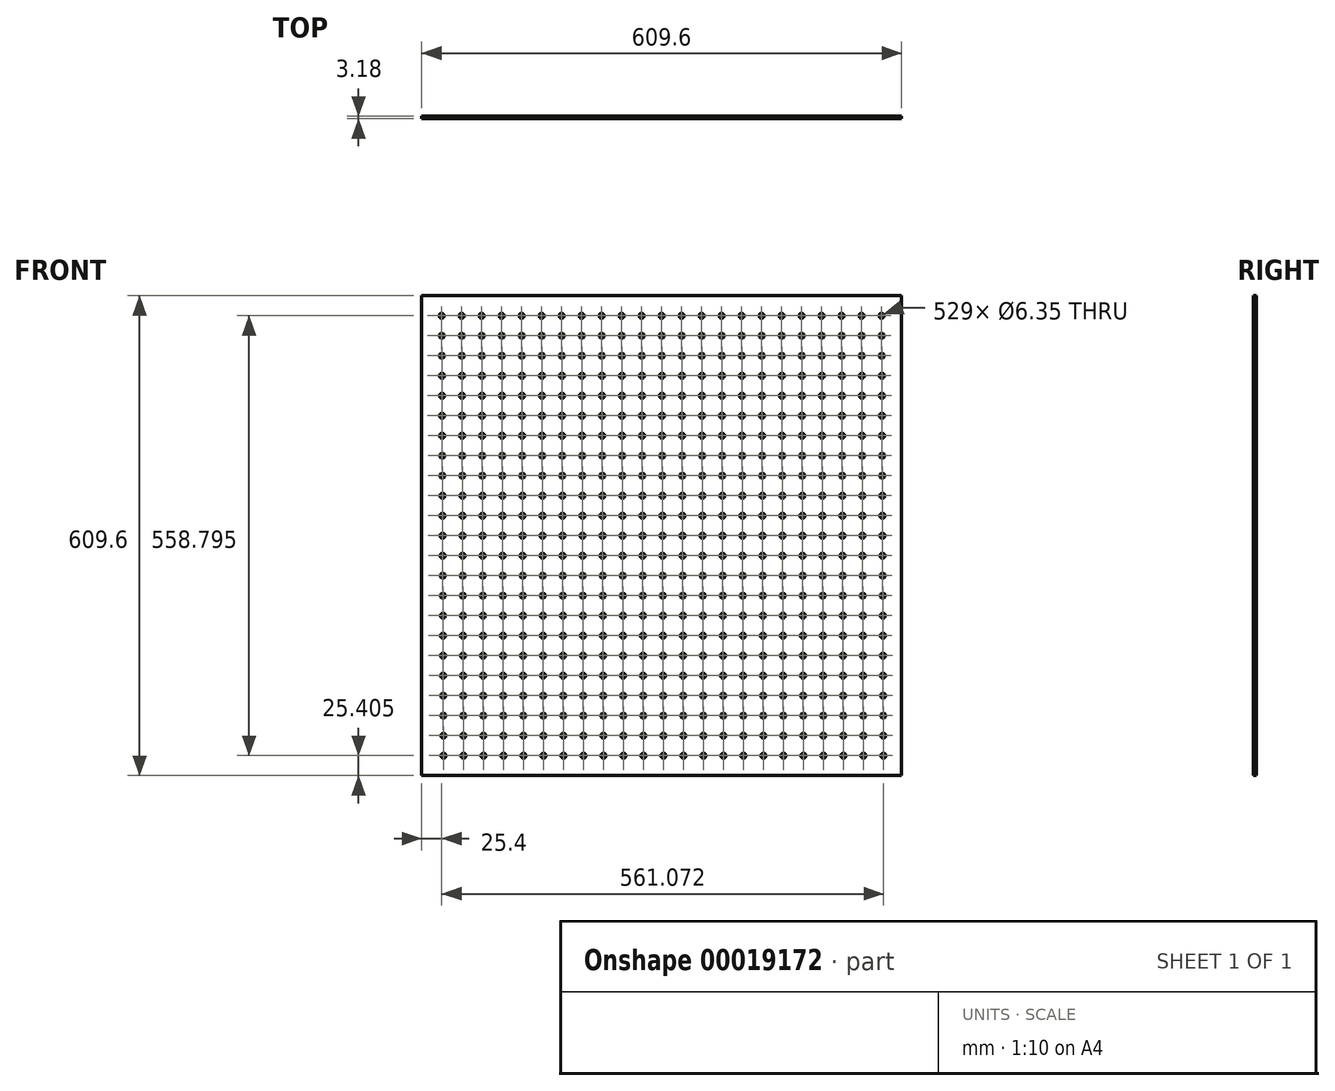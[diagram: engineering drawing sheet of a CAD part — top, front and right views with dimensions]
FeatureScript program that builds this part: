
annotation { "Feature Type Name" : "Feature", "Feature Type Description" : "" }
export const myFeature = defineFeature(function(context is Context, id is Id, definition is map)
    precondition{}
    {
        {
            var Q0;
            Q0=qCreatedBy(makeId("Front.planeOp"),FACE);
            var sketch = newSketch(context, id + "F0", { "sketchPlane" : qUnion([Q0])});
            skLineSegment(sketch, "E0.rect.bottom", {"start": v(304.8, 304.8) * mm, "end": v(-304.8, 304.8) * mm});
            skLineSegment(sketch, "E0.rect.top", {"start": v(304.8, -304.8) * mm, "end": v(-304.8, -304.8) * mm});
            skLineSegment(sketch, "E0.rect.left", {"start": v(304.8, 304.8) * mm, "end": v(304.8, -304.8) * mm});
            skLineSegment(sketch, "E0.rect.right", {"start": v(-304.8, 304.8) * mm, "end": v(-304.8, -304.8) * mm});
            skPoint(sketch, "E0.rect.middle", {"position": v(0, 0) * mm});
            skCircle(sketch, "E1", {"center": v(-279.4, 279.4) * mm, "radius": 3.18 * mm});
            skCircle(sketch, "E2.0.1.0", {"center": v(-279.3, 254) * mm, "radius": 3.18 * mm});
            skCircle(sketch, "E2.0.2.0", {"center": v(-279.2, 228.6) * mm, "radius": 3.18 * mm});
            skCircle(sketch, "E2.0.3.0", {"center": v(-279.1, 203.2) * mm, "radius": 3.18 * mm});
            skCircle(sketch, "E2.0.4.0", {"center": v(-278.99, 177.8) * mm, "radius": 3.18 * mm});
            skCircle(sketch, "E2.0.5.0", {"center": v(-278.88, 152.4) * mm, "radius": 3.18 * mm});
            skCircle(sketch, "E2.0.6.0", {"center": v(-278.78, 127) * mm, "radius": 3.18 * mm});
            skCircle(sketch, "E2.0.7.0", {"center": v(-278.68, 101.6) * mm, "radius": 3.18 * mm});
            skCircle(sketch, "E2.0.8.0", {"center": v(-278.57, 76.2) * mm, "radius": 3.18 * mm});
            skCircle(sketch, "E2.0.9.0", {"center": v(-278.47, 50.8) * mm, "radius": 3.18 * mm});
            skCircle(sketch, "E2.0.10.0", {"center": v(-278.37, 25.4) * mm, "radius": 3.18 * mm});
            skCircle(sketch, "E2.0.11.0", {"center": v(-278.26, 0) * mm, "radius": 3.18 * mm});
            skCircle(sketch, "E2.0.12.0", {"center": v(-278.16, -25.4) * mm, "radius": 3.18 * mm});
            skCircle(sketch, "E2.0.13.0", {"center": v(-278.06, -50.8) * mm, "radius": 3.18 * mm});
            skCircle(sketch, "E2.0.14.0", {"center": v(-277.95, -76.2) * mm, "radius": 3.18 * mm});
            skCircle(sketch, "E2.0.15.0", {"center": v(-277.85, -101.6) * mm, "radius": 3.18 * mm});
            skCircle(sketch, "E2.0.16.0", {"center": v(-277.75, -127) * mm, "radius": 3.18 * mm});
            skCircle(sketch, "E2.0.17.0", {"center": v(-277.64, -152.4) * mm, "radius": 3.18 * mm});
            skCircle(sketch, "E2.0.18.0", {"center": v(-277.54, -177.8) * mm, "radius": 3.18 * mm});
            skCircle(sketch, "E2.0.19.0", {"center": v(-277.44, -203.2) * mm, "radius": 3.18 * mm});
            skCircle(sketch, "E2.0.20.0", {"center": v(-277.33, -228.6) * mm, "radius": 3.18 * mm});
            skCircle(sketch, "E2.0.21.0", {"center": v(-277.23, -254) * mm, "radius": 3.18 * mm});
            skCircle(sketch, "E2.0.22.0", {"center": v(-277.13, -279.4) * mm, "radius": 3.18 * mm});
            skCircle(sketch, "E2.1.0.0", {"center": v(-254, 279.4) * mm, "radius": 3.18 * mm});
            skCircle(sketch, "E2.1.1.0", {"center": v(-253.9, 254) * mm, "radius": 3.18 * mm});
            skCircle(sketch, "E2.1.2.0", {"center": v(-253.8, 228.6) * mm, "radius": 3.18 * mm});
            skCircle(sketch, "E2.1.3.0", {"center": v(-253.7, 203.2) * mm, "radius": 3.18 * mm});
            skCircle(sketch, "E2.1.4.0", {"center": v(-253.59, 177.8) * mm, "radius": 3.18 * mm});
            skCircle(sketch, "E2.1.5.0", {"center": v(-253.48, 152.4) * mm, "radius": 3.18 * mm});
            skCircle(sketch, "E2.1.6.0", {"center": v(-253.38, 127) * mm, "radius": 3.18 * mm});
            skCircle(sketch, "E2.1.7.0", {"center": v(-253.28, 101.6) * mm, "radius": 3.18 * mm});
            skCircle(sketch, "E2.1.8.0", {"center": v(-253.17, 76.2) * mm, "radius": 3.18 * mm});
            skCircle(sketch, "E2.1.9.0", {"center": v(-253.07, 50.8) * mm, "radius": 3.18 * mm});
            skCircle(sketch, "E2.1.10.0", {"center": v(-252.97, 25.4) * mm, "radius": 3.18 * mm});
            skCircle(sketch, "E2.1.11.0", {"center": v(-252.86, 0) * mm, "radius": 3.18 * mm});
            skCircle(sketch, "E2.1.12.0", {"center": v(-252.76, -25.4) * mm, "radius": 3.18 * mm});
            skCircle(sketch, "E2.1.13.0", {"center": v(-252.66, -50.8) * mm, "radius": 3.18 * mm});
            skCircle(sketch, "E2.1.14.0", {"center": v(-252.55, -76.2) * mm, "radius": 3.18 * mm});
            skCircle(sketch, "E2.1.15.0", {"center": v(-252.45, -101.6) * mm, "radius": 3.18 * mm});
            skCircle(sketch, "E2.1.16.0", {"center": v(-252.35, -127) * mm, "radius": 3.18 * mm});
            skCircle(sketch, "E2.1.17.0", {"center": v(-252.24, -152.4) * mm, "radius": 3.18 * mm});
            skCircle(sketch, "E2.1.18.0", {"center": v(-252.14, -177.8) * mm, "radius": 3.18 * mm});
            skCircle(sketch, "E2.1.19.0", {"center": v(-252.04, -203.2) * mm, "radius": 3.18 * mm});
            skCircle(sketch, "E2.1.20.0", {"center": v(-251.93, -228.6) * mm, "radius": 3.18 * mm});
            skCircle(sketch, "E2.1.21.0", {"center": v(-251.83, -254) * mm, "radius": 3.18 * mm});
            skCircle(sketch, "E2.1.22.0", {"center": v(-251.73, -279.4) * mm, "radius": 3.18 * mm});
            skCircle(sketch, "E2.2.0.0", {"center": v(-228.6, 279.4) * mm, "radius": 3.18 * mm});
            skCircle(sketch, "E2.2.1.0", {"center": v(-228.5, 254) * mm, "radius": 3.18 * mm});
            skCircle(sketch, "E2.2.2.0", {"center": v(-228.4, 228.6) * mm, "radius": 3.18 * mm});
            skCircle(sketch, "E2.2.3.0", {"center": v(-228.3, 203.2) * mm, "radius": 3.18 * mm});
            skCircle(sketch, "E2.2.4.0", {"center": v(-228.19, 177.8) * mm, "radius": 3.18 * mm});
            skCircle(sketch, "E2.2.5.0", {"center": v(-228.08, 152.4) * mm, "radius": 3.18 * mm});
            skCircle(sketch, "E2.2.6.0", {"center": v(-227.98, 127) * mm, "radius": 3.18 * mm});
            skCircle(sketch, "E2.2.7.0", {"center": v(-227.88, 101.6) * mm, "radius": 3.18 * mm});
            skCircle(sketch, "E2.2.8.0", {"center": v(-227.77, 76.2) * mm, "radius": 3.18 * mm});
            skCircle(sketch, "E2.2.9.0", {"center": v(-227.67, 50.8) * mm, "radius": 3.18 * mm});
            skCircle(sketch, "E2.2.10.0", {"center": v(-227.57, 25.4) * mm, "radius": 3.18 * mm});
            skCircle(sketch, "E2.2.11.0", {"center": v(-227.46, 0) * mm, "radius": 3.18 * mm});
            skCircle(sketch, "E2.2.12.0", {"center": v(-227.36, -25.4) * mm, "radius": 3.18 * mm});
            skCircle(sketch, "E2.2.13.0", {"center": v(-227.26, -50.8) * mm, "radius": 3.18 * mm});
            skCircle(sketch, "E2.2.14.0", {"center": v(-227.15, -76.2) * mm, "radius": 3.18 * mm});
            skCircle(sketch, "E2.2.15.0", {"center": v(-227.05, -101.6) * mm, "radius": 3.18 * mm});
            skCircle(sketch, "E2.2.16.0", {"center": v(-226.95, -127) * mm, "radius": 3.18 * mm});
            skCircle(sketch, "E2.2.17.0", {"center": v(-226.84, -152.4) * mm, "radius": 3.18 * mm});
            skCircle(sketch, "E2.2.18.0", {"center": v(-226.74, -177.8) * mm, "radius": 3.18 * mm});
            skCircle(sketch, "E2.2.19.0", {"center": v(-226.64, -203.2) * mm, "radius": 3.18 * mm});
            skCircle(sketch, "E2.2.20.0", {"center": v(-226.53, -228.6) * mm, "radius": 3.18 * mm});
            skCircle(sketch, "E2.2.21.0", {"center": v(-226.43, -254) * mm, "radius": 3.18 * mm});
            skCircle(sketch, "E2.2.22.0", {"center": v(-226.33, -279.4) * mm, "radius": 3.18 * mm});
            skCircle(sketch, "E2.3.0.0", {"center": v(-203.2, 279.4) * mm, "radius": 3.18 * mm});
            skCircle(sketch, "E2.3.1.0", {"center": v(-203.1, 254) * mm, "radius": 3.18 * mm});
            skCircle(sketch, "E2.3.2.0", {"center": v(-203, 228.6) * mm, "radius": 3.18 * mm});
            skCircle(sketch, "E2.3.3.0", {"center": v(-202.9, 203.2) * mm, "radius": 3.18 * mm});
            skCircle(sketch, "E2.3.4.0", {"center": v(-202.79, 177.8) * mm, "radius": 3.18 * mm});
            skCircle(sketch, "E2.3.5.0", {"center": v(-202.68, 152.4) * mm, "radius": 3.18 * mm});
            skCircle(sketch, "E2.3.6.0", {"center": v(-202.58, 127) * mm, "radius": 3.18 * mm});
            skCircle(sketch, "E2.3.7.0", {"center": v(-202.48, 101.6) * mm, "radius": 3.18 * mm});
            skCircle(sketch, "E2.3.8.0", {"center": v(-202.37, 76.2) * mm, "radius": 3.18 * mm});
            skCircle(sketch, "E2.3.9.0", {"center": v(-202.27, 50.8) * mm, "radius": 3.18 * mm});
            skCircle(sketch, "E2.3.10.0", {"center": v(-202.17, 25.4) * mm, "radius": 3.18 * mm});
            skCircle(sketch, "E2.3.11.0", {"center": v(-202.06, 0) * mm, "radius": 3.18 * mm});
            skCircle(sketch, "E2.3.12.0", {"center": v(-201.96, -25.4) * mm, "radius": 3.18 * mm});
            skCircle(sketch, "E2.3.13.0", {"center": v(-201.86, -50.8) * mm, "radius": 3.18 * mm});
            skCircle(sketch, "E2.3.14.0", {"center": v(-201.75, -76.2) * mm, "radius": 3.18 * mm});
            skCircle(sketch, "E2.3.15.0", {"center": v(-201.65, -101.6) * mm, "radius": 3.18 * mm});
            skCircle(sketch, "E2.3.16.0", {"center": v(-201.55, -127) * mm, "radius": 3.18 * mm});
            skCircle(sketch, "E2.3.17.0", {"center": v(-201.44, -152.4) * mm, "radius": 3.18 * mm});
            skCircle(sketch, "E2.3.18.0", {"center": v(-201.34, -177.8) * mm, "radius": 3.18 * mm});
            skCircle(sketch, "E2.3.19.0", {"center": v(-201.24, -203.2) * mm, "radius": 3.18 * mm});
            skCircle(sketch, "E2.3.20.0", {"center": v(-201.13, -228.6) * mm, "radius": 3.18 * mm});
            skCircle(sketch, "E2.3.21.0", {"center": v(-201.03, -254) * mm, "radius": 3.18 * mm});
            skCircle(sketch, "E2.3.22.0", {"center": v(-200.93, -279.4) * mm, "radius": 3.18 * mm});
            skCircle(sketch, "E2.4.0.0", {"center": v(-177.8, 279.4) * mm, "radius": 3.18 * mm});
            skCircle(sketch, "E2.4.1.0", {"center": v(-177.7, 254) * mm, "radius": 3.18 * mm});
            skCircle(sketch, "E2.4.2.0", {"center": v(-177.6, 228.6) * mm, "radius": 3.18 * mm});
            skCircle(sketch, "E2.4.3.0", {"center": v(-177.5, 203.2) * mm, "radius": 3.18 * mm});
            skCircle(sketch, "E2.4.4.0", {"center": v(-177.39, 177.8) * mm, "radius": 3.18 * mm});
            skCircle(sketch, "E2.4.5.0", {"center": v(-177.28, 152.4) * mm, "radius": 3.18 * mm});
            skCircle(sketch, "E2.4.6.0", {"center": v(-177.18, 127) * mm, "radius": 3.18 * mm});
            skCircle(sketch, "E2.4.7.0", {"center": v(-177.08, 101.6) * mm, "radius": 3.18 * mm});
            skCircle(sketch, "E2.4.8.0", {"center": v(-176.97, 76.2) * mm, "radius": 3.18 * mm});
            skCircle(sketch, "E2.4.9.0", {"center": v(-176.87, 50.8) * mm, "radius": 3.18 * mm});
            skCircle(sketch, "E2.4.10.0", {"center": v(-176.77, 25.4) * mm, "radius": 3.18 * mm});
            skCircle(sketch, "E2.4.11.0", {"center": v(-176.66, 0) * mm, "radius": 3.18 * mm});
            skCircle(sketch, "E2.4.12.0", {"center": v(-176.56, -25.4) * mm, "radius": 3.18 * mm});
            skCircle(sketch, "E2.4.13.0", {"center": v(-176.46, -50.8) * mm, "radius": 3.18 * mm});
            skCircle(sketch, "E2.4.14.0", {"center": v(-176.35, -76.2) * mm, "radius": 3.18 * mm});
            skCircle(sketch, "E2.4.15.0", {"center": v(-176.25, -101.6) * mm, "radius": 3.18 * mm});
            skCircle(sketch, "E2.4.16.0", {"center": v(-176.15, -127) * mm, "radius": 3.18 * mm});
            skCircle(sketch, "E2.4.17.0", {"center": v(-176.04, -152.4) * mm, "radius": 3.18 * mm});
            skCircle(sketch, "E2.4.18.0", {"center": v(-175.94, -177.8) * mm, "radius": 3.18 * mm});
            skCircle(sketch, "E2.4.19.0", {"center": v(-175.84, -203.2) * mm, "radius": 3.18 * mm});
            skCircle(sketch, "E2.4.20.0", {"center": v(-175.73, -228.6) * mm, "radius": 3.18 * mm});
            skCircle(sketch, "E2.4.21.0", {"center": v(-175.63, -254) * mm, "radius": 3.18 * mm});
            skCircle(sketch, "E2.4.22.0", {"center": v(-175.53, -279.4) * mm, "radius": 3.18 * mm});
            skCircle(sketch, "E2.5.0.0", {"center": v(-152.4, 279.4) * mm, "radius": 3.18 * mm});
            skCircle(sketch, "E2.5.1.0", {"center": v(-152.3, 254) * mm, "radius": 3.18 * mm});
            skCircle(sketch, "E2.5.2.0", {"center": v(-152.2, 228.6) * mm, "radius": 3.18 * mm});
            skCircle(sketch, "E2.5.3.0", {"center": v(-152.1, 203.2) * mm, "radius": 3.18 * mm});
            skCircle(sketch, "E2.5.4.0", {"center": v(-151.99, 177.8) * mm, "radius": 3.18 * mm});
            skCircle(sketch, "E2.5.5.0", {"center": v(-151.88, 152.4) * mm, "radius": 3.18 * mm});
            skCircle(sketch, "E2.5.6.0", {"center": v(-151.78, 127) * mm, "radius": 3.18 * mm});
            skCircle(sketch, "E2.5.7.0", {"center": v(-151.68, 101.6) * mm, "radius": 3.18 * mm});
            skCircle(sketch, "E2.5.8.0", {"center": v(-151.57, 76.2) * mm, "radius": 3.18 * mm});
            skCircle(sketch, "E2.5.9.0", {"center": v(-151.47, 50.8) * mm, "radius": 3.18 * mm});
            skCircle(sketch, "E2.5.10.0", {"center": v(-151.37, 25.4) * mm, "radius": 3.18 * mm});
            skCircle(sketch, "E2.5.11.0", {"center": v(-151.26, 0) * mm, "radius": 3.18 * mm});
            skCircle(sketch, "E2.5.12.0", {"center": v(-151.16, -25.4) * mm, "radius": 3.18 * mm});
            skCircle(sketch, "E2.5.13.0", {"center": v(-151.06, -50.8) * mm, "radius": 3.18 * mm});
            skCircle(sketch, "E2.5.14.0", {"center": v(-150.95, -76.2) * mm, "radius": 3.18 * mm});
            skCircle(sketch, "E2.5.15.0", {"center": v(-150.85, -101.6) * mm, "radius": 3.18 * mm});
            skCircle(sketch, "E2.5.16.0", {"center": v(-150.75, -127) * mm, "radius": 3.18 * mm});
            skCircle(sketch, "E2.5.17.0", {"center": v(-150.64, -152.4) * mm, "radius": 3.18 * mm});
            skCircle(sketch, "E2.5.18.0", {"center": v(-150.54, -177.8) * mm, "radius": 3.18 * mm});
            skCircle(sketch, "E2.5.19.0", {"center": v(-150.44, -203.2) * mm, "radius": 3.18 * mm});
            skCircle(sketch, "E2.5.20.0", {"center": v(-150.33, -228.6) * mm, "radius": 3.18 * mm});
            skCircle(sketch, "E2.5.21.0", {"center": v(-150.23, -254) * mm, "radius": 3.18 * mm});
            skCircle(sketch, "E2.5.22.0", {"center": v(-150.13, -279.4) * mm, "radius": 3.18 * mm});
            skCircle(sketch, "E2.6.0.0", {"center": v(-127, 279.4) * mm, "radius": 3.18 * mm});
            skCircle(sketch, "E2.6.1.0", {"center": v(-126.9, 254) * mm, "radius": 3.18 * mm});
            skCircle(sketch, "E2.6.2.0", {"center": v(-126.8, 228.6) * mm, "radius": 3.18 * mm});
            skCircle(sketch, "E2.6.3.0", {"center": v(-126.7, 203.2) * mm, "radius": 3.18 * mm});
            skCircle(sketch, "E2.6.4.0", {"center": v(-126.59, 177.8) * mm, "radius": 3.18 * mm});
            skCircle(sketch, "E2.6.5.0", {"center": v(-126.48, 152.4) * mm, "radius": 3.18 * mm});
            skCircle(sketch, "E2.6.6.0", {"center": v(-126.38, 127) * mm, "radius": 3.18 * mm});
            skCircle(sketch, "E2.6.7.0", {"center": v(-126.28, 101.6) * mm, "radius": 3.18 * mm});
            skCircle(sketch, "E2.6.8.0", {"center": v(-126.17, 76.2) * mm, "radius": 3.18 * mm});
            skCircle(sketch, "E2.6.9.0", {"center": v(-126.07, 50.8) * mm, "radius": 3.18 * mm});
            skCircle(sketch, "E2.6.10.0", {"center": v(-125.97, 25.4) * mm, "radius": 3.18 * mm});
            skCircle(sketch, "E2.6.11.0", {"center": v(-125.86, 0) * mm, "radius": 3.18 * mm});
            skCircle(sketch, "E2.6.12.0", {"center": v(-125.76, -25.4) * mm, "radius": 3.18 * mm});
            skCircle(sketch, "E2.6.13.0", {"center": v(-125.66, -50.8) * mm, "radius": 3.18 * mm});
            skCircle(sketch, "E2.6.14.0", {"center": v(-125.55, -76.2) * mm, "radius": 3.18 * mm});
            skCircle(sketch, "E2.6.15.0", {"center": v(-125.45, -101.6) * mm, "radius": 3.18 * mm});
            skCircle(sketch, "E2.6.16.0", {"center": v(-125.35, -127) * mm, "radius": 3.18 * mm});
            skCircle(sketch, "E2.6.17.0", {"center": v(-125.24, -152.4) * mm, "radius": 3.18 * mm});
            skCircle(sketch, "E2.6.18.0", {"center": v(-125.14, -177.8) * mm, "radius": 3.18 * mm});
            skCircle(sketch, "E2.6.19.0", {"center": v(-125.04, -203.2) * mm, "radius": 3.18 * mm});
            skCircle(sketch, "E2.6.20.0", {"center": v(-124.93, -228.6) * mm, "radius": 3.18 * mm});
            skCircle(sketch, "E2.6.21.0", {"center": v(-124.83, -254) * mm, "radius": 3.18 * mm});
            skCircle(sketch, "E2.6.22.0", {"center": v(-124.73, -279.4) * mm, "radius": 3.18 * mm});
            skCircle(sketch, "E2.7.0.0", {"center": v(-101.6, 279.4) * mm, "radius": 3.18 * mm});
            skCircle(sketch, "E2.7.1.0", {"center": v(-101.5, 254) * mm, "radius": 3.18 * mm});
            skCircle(sketch, "E2.7.2.0", {"center": v(-101.4, 228.6) * mm, "radius": 3.18 * mm});
            skCircle(sketch, "E2.7.3.0", {"center": v(-101.3, 203.2) * mm, "radius": 3.18 * mm});
            skCircle(sketch, "E2.7.4.0", {"center": v(-101.19, 177.8) * mm, "radius": 3.18 * mm});
            skCircle(sketch, "E2.7.5.0", {"center": v(-101.08, 152.4) * mm, "radius": 3.18 * mm});
            skCircle(sketch, "E2.7.6.0", {"center": v(-100.98, 127) * mm, "radius": 3.18 * mm});
            skCircle(sketch, "E2.7.7.0", {"center": v(-100.88, 101.6) * mm, "radius": 3.18 * mm});
            skCircle(sketch, "E2.7.8.0", {"center": v(-100.77, 76.2) * mm, "radius": 3.18 * mm});
            skCircle(sketch, "E2.7.9.0", {"center": v(-100.67, 50.8) * mm, "radius": 3.18 * mm});
            skCircle(sketch, "E2.7.10.0", {"center": v(-100.57, 25.4) * mm, "radius": 3.18 * mm});
            skCircle(sketch, "E2.7.11.0", {"center": v(-100.46, 0) * mm, "radius": 3.18 * mm});
            skCircle(sketch, "E2.7.12.0", {"center": v(-100.36, -25.4) * mm, "radius": 3.18 * mm});
            skCircle(sketch, "E2.7.13.0", {"center": v(-100.26, -50.8) * mm, "radius": 3.18 * mm});
            skCircle(sketch, "E2.7.14.0", {"center": v(-100.15, -76.2) * mm, "radius": 3.18 * mm});
            skCircle(sketch, "E2.7.15.0", {"center": v(-100.05, -101.6) * mm, "radius": 3.18 * mm});
            skCircle(sketch, "E2.7.16.0", {"center": v(-99.95, -127) * mm, "radius": 3.18 * mm});
            skCircle(sketch, "E2.7.17.0", {"center": v(-99.84, -152.4) * mm, "radius": 3.18 * mm});
            skCircle(sketch, "E2.7.18.0", {"center": v(-99.74, -177.8) * mm, "radius": 3.18 * mm});
            skCircle(sketch, "E2.7.19.0", {"center": v(-99.64, -203.2) * mm, "radius": 3.18 * mm});
            skCircle(sketch, "E2.7.20.0", {"center": v(-99.53, -228.6) * mm, "radius": 3.18 * mm});
            skCircle(sketch, "E2.7.21.0", {"center": v(-99.43, -254) * mm, "radius": 3.18 * mm});
            skCircle(sketch, "E2.7.22.0", {"center": v(-99.33, -279.4) * mm, "radius": 3.18 * mm});
            skCircle(sketch, "E2.8.0.0", {"center": v(-76.2, 279.4) * mm, "radius": 3.18 * mm});
            skCircle(sketch, "E2.8.1.0", {"center": v(-76.1, 254) * mm, "radius": 3.18 * mm});
            skCircle(sketch, "E2.8.2.0", {"center": v(-76, 228.6) * mm, "radius": 3.18 * mm});
            skCircle(sketch, "E2.8.3.0", {"center": v(-75.9, 203.2) * mm, "radius": 3.18 * mm});
            skCircle(sketch, "E2.8.4.0", {"center": v(-75.79, 177.8) * mm, "radius": 3.18 * mm});
            skCircle(sketch, "E2.8.5.0", {"center": v(-75.68, 152.4) * mm, "radius": 3.18 * mm});
            skCircle(sketch, "E2.8.6.0", {"center": v(-75.58, 127) * mm, "radius": 3.18 * mm});
            skCircle(sketch, "E2.8.7.0", {"center": v(-75.48, 101.6) * mm, "radius": 3.18 * mm});
            skCircle(sketch, "E2.8.8.0", {"center": v(-75.37, 76.2) * mm, "radius": 3.18 * mm});
            skCircle(sketch, "E2.8.9.0", {"center": v(-75.27, 50.8) * mm, "radius": 3.18 * mm});
            skCircle(sketch, "E2.8.10.0", {"center": v(-75.17, 25.4) * mm, "radius": 3.18 * mm});
            skCircle(sketch, "E2.8.11.0", {"center": v(-75.06, 0) * mm, "radius": 3.18 * mm});
            skCircle(sketch, "E2.8.12.0", {"center": v(-74.96, -25.4) * mm, "radius": 3.18 * mm});
            skCircle(sketch, "E2.8.13.0", {"center": v(-74.86, -50.8) * mm, "radius": 3.18 * mm});
            skCircle(sketch, "E2.8.14.0", {"center": v(-74.75, -76.2) * mm, "radius": 3.18 * mm});
            skCircle(sketch, "E2.8.15.0", {"center": v(-74.65, -101.6) * mm, "radius": 3.18 * mm});
            skCircle(sketch, "E2.8.16.0", {"center": v(-74.55, -127) * mm, "radius": 3.18 * mm});
            skCircle(sketch, "E2.8.17.0", {"center": v(-74.44, -152.4) * mm, "radius": 3.18 * mm});
            skCircle(sketch, "E2.8.18.0", {"center": v(-74.34, -177.8) * mm, "radius": 3.18 * mm});
            skCircle(sketch, "E2.8.19.0", {"center": v(-74.24, -203.2) * mm, "radius": 3.18 * mm});
            skCircle(sketch, "E2.8.20.0", {"center": v(-74.13, -228.6) * mm, "radius": 3.18 * mm});
            skCircle(sketch, "E2.8.21.0", {"center": v(-74.03, -254) * mm, "radius": 3.18 * mm});
            skCircle(sketch, "E2.8.22.0", {"center": v(-73.93, -279.4) * mm, "radius": 3.18 * mm});
            skCircle(sketch, "E2.9.0.0", {"center": v(-50.8, 279.4) * mm, "radius": 3.18 * mm});
            skCircle(sketch, "E2.9.1.0", {"center": v(-50.7, 254) * mm, "radius": 3.18 * mm});
            skCircle(sketch, "E2.9.2.0", {"center": v(-50.6, 228.6) * mm, "radius": 3.18 * mm});
            skCircle(sketch, "E2.9.3.0", {"center": v(-50.5, 203.2) * mm, "radius": 3.18 * mm});
            skCircle(sketch, "E2.9.4.0", {"center": v(-50.39, 177.8) * mm, "radius": 3.18 * mm});
            skCircle(sketch, "E2.9.5.0", {"center": v(-50.28, 152.4) * mm, "radius": 3.18 * mm});
            skCircle(sketch, "E2.9.6.0", {"center": v(-50.18, 127) * mm, "radius": 3.18 * mm});
            skCircle(sketch, "E2.9.7.0", {"center": v(-50.08, 101.6) * mm, "radius": 3.18 * mm});
            skCircle(sketch, "E2.9.8.0", {"center": v(-49.97, 76.2) * mm, "radius": 3.18 * mm});
            skCircle(sketch, "E2.9.9.0", {"center": v(-49.87, 50.8) * mm, "radius": 3.18 * mm});
            skCircle(sketch, "E2.9.10.0", {"center": v(-49.77, 25.4) * mm, "radius": 3.18 * mm});
            skCircle(sketch, "E2.9.11.0", {"center": v(-49.66, 0) * mm, "radius": 3.18 * mm});
            skCircle(sketch, "E2.9.12.0", {"center": v(-49.56, -25.4) * mm, "radius": 3.18 * mm});
            skCircle(sketch, "E2.9.13.0", {"center": v(-49.46, -50.8) * mm, "radius": 3.18 * mm});
            skCircle(sketch, "E2.9.14.0", {"center": v(-49.35, -76.2) * mm, "radius": 3.18 * mm});
            skCircle(sketch, "E2.9.15.0", {"center": v(-49.25, -101.6) * mm, "radius": 3.18 * mm});
            skCircle(sketch, "E2.9.16.0", {"center": v(-49.15, -127) * mm, "radius": 3.18 * mm});
            skCircle(sketch, "E2.9.17.0", {"center": v(-49.04, -152.4) * mm, "radius": 3.18 * mm});
            skCircle(sketch, "E2.9.18.0", {"center": v(-48.94, -177.8) * mm, "radius": 3.18 * mm});
            skCircle(sketch, "E2.9.19.0", {"center": v(-48.84, -203.2) * mm, "radius": 3.18 * mm});
            skCircle(sketch, "E2.9.20.0", {"center": v(-48.73, -228.6) * mm, "radius": 3.18 * mm});
            skCircle(sketch, "E2.9.21.0", {"center": v(-48.63, -254) * mm, "radius": 3.18 * mm});
            skCircle(sketch, "E2.9.22.0", {"center": v(-48.53, -279.4) * mm, "radius": 3.18 * mm});
            skCircle(sketch, "E2.10.0.0", {"center": v(-25.4, 279.4) * mm, "radius": 3.18 * mm});
            skCircle(sketch, "E2.10.1.0", {"center": v(-25.3, 254) * mm, "radius": 3.18 * mm});
            skCircle(sketch, "E2.10.2.0", {"center": v(-25.2, 228.6) * mm, "radius": 3.18 * mm});
            skCircle(sketch, "E2.10.3.0", {"center": v(-25.1, 203.2) * mm, "radius": 3.18 * mm});
            skCircle(sketch, "E2.10.4.0", {"center": v(-24.99, 177.8) * mm, "radius": 3.18 * mm});
            skCircle(sketch, "E2.10.5.0", {"center": v(-24.88, 152.4) * mm, "radius": 3.18 * mm});
            skCircle(sketch, "E2.10.6.0", {"center": v(-24.78, 127) * mm, "radius": 3.18 * mm});
            skCircle(sketch, "E2.10.7.0", {"center": v(-24.68, 101.6) * mm, "radius": 3.18 * mm});
            skCircle(sketch, "E2.10.8.0", {"center": v(-24.57, 76.2) * mm, "radius": 3.18 * mm});
            skCircle(sketch, "E2.10.9.0", {"center": v(-24.47, 50.8) * mm, "radius": 3.18 * mm});
            skCircle(sketch, "E2.10.10.0", {"center": v(-24.37, 25.4) * mm, "radius": 3.18 * mm});
            skCircle(sketch, "E2.10.11.0", {"center": v(-24.26, 0) * mm, "radius": 3.18 * mm});
            skCircle(sketch, "E2.10.12.0", {"center": v(-24.16, -25.4) * mm, "radius": 3.18 * mm});
            skCircle(sketch, "E2.10.13.0", {"center": v(-24.06, -50.8) * mm, "radius": 3.18 * mm});
            skCircle(sketch, "E2.10.14.0", {"center": v(-23.95, -76.2) * mm, "radius": 3.18 * mm});
            skCircle(sketch, "E2.10.15.0", {"center": v(-23.85, -101.6) * mm, "radius": 3.18 * mm});
            skCircle(sketch, "E2.10.16.0", {"center": v(-23.75, -127) * mm, "radius": 3.18 * mm});
            skCircle(sketch, "E2.10.17.0", {"center": v(-23.64, -152.4) * mm, "radius": 3.18 * mm});
            skCircle(sketch, "E2.10.18.0", {"center": v(-23.54, -177.8) * mm, "radius": 3.18 * mm});
            skCircle(sketch, "E2.10.19.0", {"center": v(-23.44, -203.2) * mm, "radius": 3.18 * mm});
            skCircle(sketch, "E2.10.20.0", {"center": v(-23.33, -228.6) * mm, "radius": 3.18 * mm});
            skCircle(sketch, "E2.10.21.0", {"center": v(-23.23, -254) * mm, "radius": 3.18 * mm});
            skCircle(sketch, "E2.10.22.0", {"center": v(-23.13, -279.4) * mm, "radius": 3.18 * mm});
            skCircle(sketch, "E2.11.0.0", {"center": v(0, 279.4) * mm, "radius": 3.18 * mm});
            skCircle(sketch, "E2.11.1.0", {"center": v(0.1, 254) * mm, "radius": 3.18 * mm});
            skCircle(sketch, "E2.11.2.0", {"center": v(0.2, 228.6) * mm, "radius": 3.18 * mm});
            skCircle(sketch, "E2.11.3.0", {"center": v(0.3, 203.2) * mm, "radius": 3.18 * mm});
            skCircle(sketch, "E2.11.4.0", {"center": v(0.41, 177.8) * mm, "radius": 3.18 * mm});
            skCircle(sketch, "E2.11.5.0", {"center": v(0.52, 152.4) * mm, "radius": 3.18 * mm});
            skCircle(sketch, "E2.11.6.0", {"center": v(0.62, 127) * mm, "radius": 3.18 * mm});
            skCircle(sketch, "E2.11.7.0", {"center": v(0.72, 101.6) * mm, "radius": 3.18 * mm});
            skCircle(sketch, "E2.11.8.0", {"center": v(0.83, 76.2) * mm, "radius": 3.18 * mm});
            skCircle(sketch, "E2.11.9.0", {"center": v(0.93, 50.8) * mm, "radius": 3.18 * mm});
            skCircle(sketch, "E2.11.10.0", {"center": v(1.03, 25.4) * mm, "radius": 3.18 * mm});
            skCircle(sketch, "E2.11.11.0", {"center": v(1.14, 0) * mm, "radius": 3.18 * mm});
            skCircle(sketch, "E2.11.12.0", {"center": v(1.24, -25.4) * mm, "radius": 3.18 * mm});
            skCircle(sketch, "E2.11.13.0", {"center": v(1.34, -50.8) * mm, "radius": 3.18 * mm});
            skCircle(sketch, "E2.11.14.0", {"center": v(1.45, -76.2) * mm, "radius": 3.18 * mm});
            skCircle(sketch, "E2.11.15.0", {"center": v(1.55, -101.6) * mm, "radius": 3.18 * mm});
            skCircle(sketch, "E2.11.16.0", {"center": v(1.65, -127) * mm, "radius": 3.18 * mm});
            skCircle(sketch, "E2.11.17.0", {"center": v(1.76, -152.4) * mm, "radius": 3.18 * mm});
            skCircle(sketch, "E2.11.18.0", {"center": v(1.86, -177.8) * mm, "radius": 3.18 * mm});
            skCircle(sketch, "E2.11.19.0", {"center": v(1.96, -203.2) * mm, "radius": 3.18 * mm});
            skCircle(sketch, "E2.11.20.0", {"center": v(2.07, -228.6) * mm, "radius": 3.18 * mm});
            skCircle(sketch, "E2.11.21.0", {"center": v(2.17, -254) * mm, "radius": 3.18 * mm});
            skCircle(sketch, "E2.11.22.0", {"center": v(2.27, -279.4) * mm, "radius": 3.18 * mm});
            skCircle(sketch, "E2.12.0.0", {"center": v(25.4, 279.4) * mm, "radius": 3.18 * mm});
            skCircle(sketch, "E2.12.1.0", {"center": v(25.5, 254) * mm, "radius": 3.18 * mm});
            skCircle(sketch, "E2.12.2.0", {"center": v(25.6, 228.6) * mm, "radius": 3.18 * mm});
            skCircle(sketch, "E2.12.3.0", {"center": v(25.7, 203.2) * mm, "radius": 3.18 * mm});
            skCircle(sketch, "E2.12.4.0", {"center": v(25.81, 177.8) * mm, "radius": 3.18 * mm});
            skCircle(sketch, "E2.12.5.0", {"center": v(25.92, 152.4) * mm, "radius": 3.18 * mm});
            skCircle(sketch, "E2.12.6.0", {"center": v(26.02, 127) * mm, "radius": 3.18 * mm});
            skCircle(sketch, "E2.12.7.0", {"center": v(26.12, 101.6) * mm, "radius": 3.18 * mm});
            skCircle(sketch, "E2.12.8.0", {"center": v(26.23, 76.2) * mm, "radius": 3.18 * mm});
            skCircle(sketch, "E2.12.9.0", {"center": v(26.33, 50.8) * mm, "radius": 3.18 * mm});
            skCircle(sketch, "E2.12.10.0", {"center": v(26.43, 25.4) * mm, "radius": 3.18 * mm});
            skCircle(sketch, "E2.12.11.0", {"center": v(26.54, 0) * mm, "radius": 3.18 * mm});
            skCircle(sketch, "E2.12.12.0", {"center": v(26.64, -25.4) * mm, "radius": 3.18 * mm});
            skCircle(sketch, "E2.12.13.0", {"center": v(26.74, -50.8) * mm, "radius": 3.18 * mm});
            skCircle(sketch, "E2.12.14.0", {"center": v(26.85, -76.2) * mm, "radius": 3.18 * mm});
            skCircle(sketch, "E2.12.15.0", {"center": v(26.95, -101.6) * mm, "radius": 3.18 * mm});
            skCircle(sketch, "E2.12.16.0", {"center": v(27.05, -127) * mm, "radius": 3.18 * mm});
            skCircle(sketch, "E2.12.17.0", {"center": v(27.16, -152.4) * mm, "radius": 3.18 * mm});
            skCircle(sketch, "E2.12.18.0", {"center": v(27.26, -177.8) * mm, "radius": 3.18 * mm});
            skCircle(sketch, "E2.12.19.0", {"center": v(27.36, -203.2) * mm, "radius": 3.18 * mm});
            skCircle(sketch, "E2.12.20.0", {"center": v(27.47, -228.6) * mm, "radius": 3.18 * mm});
            skCircle(sketch, "E2.12.21.0", {"center": v(27.57, -254) * mm, "radius": 3.18 * mm});
            skCircle(sketch, "E2.12.22.0", {"center": v(27.67, -279.4) * mm, "radius": 3.18 * mm});
            skCircle(sketch, "E2.13.0.0", {"center": v(50.8, 279.4) * mm, "radius": 3.18 * mm});
            skCircle(sketch, "E2.13.1.0", {"center": v(50.9, 254) * mm, "radius": 3.18 * mm});
            skCircle(sketch, "E2.13.2.0", {"center": v(51, 228.6) * mm, "radius": 3.18 * mm});
            skCircle(sketch, "E2.13.3.0", {"center": v(51.1, 203.2) * mm, "radius": 3.18 * mm});
            skCircle(sketch, "E2.13.4.0", {"center": v(51.21, 177.8) * mm, "radius": 3.18 * mm});
            skCircle(sketch, "E2.13.5.0", {"center": v(51.32, 152.4) * mm, "radius": 3.18 * mm});
            skCircle(sketch, "E2.13.6.0", {"center": v(51.42, 127) * mm, "radius": 3.18 * mm});
            skCircle(sketch, "E2.13.7.0", {"center": v(51.52, 101.6) * mm, "radius": 3.18 * mm});
            skCircle(sketch, "E2.13.8.0", {"center": v(51.63, 76.2) * mm, "radius": 3.18 * mm});
            skCircle(sketch, "E2.13.9.0", {"center": v(51.73, 50.8) * mm, "radius": 3.18 * mm});
            skCircle(sketch, "E2.13.10.0", {"center": v(51.83, 25.4) * mm, "radius": 3.18 * mm});
            skCircle(sketch, "E2.13.11.0", {"center": v(51.94, 0) * mm, "radius": 3.18 * mm});
            skCircle(sketch, "E2.13.12.0", {"center": v(52.04, -25.4) * mm, "radius": 3.18 * mm});
            skCircle(sketch, "E2.13.13.0", {"center": v(52.14, -50.8) * mm, "radius": 3.18 * mm});
            skCircle(sketch, "E2.13.14.0", {"center": v(52.25, -76.2) * mm, "radius": 3.18 * mm});
            skCircle(sketch, "E2.13.15.0", {"center": v(52.35, -101.6) * mm, "radius": 3.18 * mm});
            skCircle(sketch, "E2.13.16.0", {"center": v(52.45, -127) * mm, "radius": 3.18 * mm});
            skCircle(sketch, "E2.13.17.0", {"center": v(52.56, -152.4) * mm, "radius": 3.18 * mm});
            skCircle(sketch, "E2.13.18.0", {"center": v(52.66, -177.8) * mm, "radius": 3.18 * mm});
            skCircle(sketch, "E2.13.19.0", {"center": v(52.76, -203.2) * mm, "radius": 3.18 * mm});
            skCircle(sketch, "E2.13.20.0", {"center": v(52.87, -228.6) * mm, "radius": 3.18 * mm});
            skCircle(sketch, "E2.13.21.0", {"center": v(52.97, -254) * mm, "radius": 3.18 * mm});
            skCircle(sketch, "E2.13.22.0", {"center": v(53.07, -279.4) * mm, "radius": 3.18 * mm});
            skCircle(sketch, "E2.14.0.0", {"center": v(76.2, 279.4) * mm, "radius": 3.18 * mm});
            skCircle(sketch, "E2.14.1.0", {"center": v(76.3, 254) * mm, "radius": 3.18 * mm});
            skCircle(sketch, "E2.14.2.0", {"center": v(76.4, 228.6) * mm, "radius": 3.18 * mm});
            skCircle(sketch, "E2.14.3.0", {"center": v(76.5, 203.2) * mm, "radius": 3.18 * mm});
            skCircle(sketch, "E2.14.4.0", {"center": v(76.61, 177.8) * mm, "radius": 3.18 * mm});
            skCircle(sketch, "E2.14.5.0", {"center": v(76.72, 152.4) * mm, "radius": 3.18 * mm});
            skCircle(sketch, "E2.14.6.0", {"center": v(76.82, 127) * mm, "radius": 3.18 * mm});
            skCircle(sketch, "E2.14.7.0", {"center": v(76.92, 101.6) * mm, "radius": 3.18 * mm});
            skCircle(sketch, "E2.14.8.0", {"center": v(77.03, 76.2) * mm, "radius": 3.18 * mm});
            skCircle(sketch, "E2.14.9.0", {"center": v(77.13, 50.8) * mm, "radius": 3.18 * mm});
            skCircle(sketch, "E2.14.10.0", {"center": v(77.23, 25.4) * mm, "radius": 3.18 * mm});
            skCircle(sketch, "E2.14.11.0", {"center": v(77.34, 0) * mm, "radius": 3.18 * mm});
            skCircle(sketch, "E2.14.12.0", {"center": v(77.44, -25.4) * mm, "radius": 3.18 * mm});
            skCircle(sketch, "E2.14.13.0", {"center": v(77.54, -50.8) * mm, "radius": 3.18 * mm});
            skCircle(sketch, "E2.14.14.0", {"center": v(77.65, -76.2) * mm, "radius": 3.18 * mm});
            skCircle(sketch, "E2.14.15.0", {"center": v(77.75, -101.6) * mm, "radius": 3.18 * mm});
            skCircle(sketch, "E2.14.16.0", {"center": v(77.85, -127) * mm, "radius": 3.18 * mm});
            skCircle(sketch, "E2.14.17.0", {"center": v(77.96, -152.4) * mm, "radius": 3.18 * mm});
            skCircle(sketch, "E2.14.18.0", {"center": v(78.06, -177.8) * mm, "radius": 3.18 * mm});
            skCircle(sketch, "E2.14.19.0", {"center": v(78.16, -203.2) * mm, "radius": 3.18 * mm});
            skCircle(sketch, "E2.14.20.0", {"center": v(78.27, -228.6) * mm, "radius": 3.18 * mm});
            skCircle(sketch, "E2.14.21.0", {"center": v(78.37, -254) * mm, "radius": 3.18 * mm});
            skCircle(sketch, "E2.14.22.0", {"center": v(78.47, -279.4) * mm, "radius": 3.18 * mm});
            skCircle(sketch, "E2.15.0.0", {"center": v(101.6, 279.4) * mm, "radius": 3.18 * mm});
            skCircle(sketch, "E2.15.1.0", {"center": v(101.7, 254) * mm, "radius": 3.18 * mm});
            skCircle(sketch, "E2.15.2.0", {"center": v(101.8, 228.6) * mm, "radius": 3.18 * mm});
            skCircle(sketch, "E2.15.3.0", {"center": v(101.9, 203.2) * mm, "radius": 3.18 * mm});
            skCircle(sketch, "E2.15.4.0", {"center": v(102.01, 177.8) * mm, "radius": 3.18 * mm});
            skCircle(sketch, "E2.15.5.0", {"center": v(102.12, 152.4) * mm, "radius": 3.18 * mm});
            skCircle(sketch, "E2.15.6.0", {"center": v(102.22, 127) * mm, "radius": 3.18 * mm});
            skCircle(sketch, "E2.15.7.0", {"center": v(102.32, 101.6) * mm, "radius": 3.18 * mm});
            skCircle(sketch, "E2.15.8.0", {"center": v(102.43, 76.2) * mm, "radius": 3.18 * mm});
            skCircle(sketch, "E2.15.9.0", {"center": v(102.53, 50.8) * mm, "radius": 3.18 * mm});
            skCircle(sketch, "E2.15.10.0", {"center": v(102.63, 25.4) * mm, "radius": 3.18 * mm});
            skCircle(sketch, "E2.15.11.0", {"center": v(102.74, 0) * mm, "radius": 3.18 * mm});
            skCircle(sketch, "E2.15.12.0", {"center": v(102.84, -25.4) * mm, "radius": 3.18 * mm});
            skCircle(sketch, "E2.15.13.0", {"center": v(102.94, -50.8) * mm, "radius": 3.18 * mm});
            skCircle(sketch, "E2.15.14.0", {"center": v(103.05, -76.2) * mm, "radius": 3.18 * mm});
            skCircle(sketch, "E2.15.15.0", {"center": v(103.15, -101.6) * mm, "radius": 3.18 * mm});
            skCircle(sketch, "E2.15.16.0", {"center": v(103.25, -127) * mm, "radius": 3.18 * mm});
            skCircle(sketch, "E2.15.17.0", {"center": v(103.36, -152.4) * mm, "radius": 3.18 * mm});
            skCircle(sketch, "E2.15.18.0", {"center": v(103.46, -177.8) * mm, "radius": 3.18 * mm});
            skCircle(sketch, "E2.15.19.0", {"center": v(103.56, -203.2) * mm, "radius": 3.18 * mm});
            skCircle(sketch, "E2.15.20.0", {"center": v(103.67, -228.6) * mm, "radius": 3.18 * mm});
            skCircle(sketch, "E2.15.21.0", {"center": v(103.77, -254) * mm, "radius": 3.18 * mm});
            skCircle(sketch, "E2.15.22.0", {"center": v(103.87, -279.4) * mm, "radius": 3.18 * mm});
            skCircle(sketch, "E2.16.0.0", {"center": v(127, 279.4) * mm, "radius": 3.18 * mm});
            skCircle(sketch, "E2.16.1.0", {"center": v(127.1, 254) * mm, "radius": 3.18 * mm});
            skCircle(sketch, "E2.16.2.0", {"center": v(127.2, 228.6) * mm, "radius": 3.18 * mm});
            skCircle(sketch, "E2.16.3.0", {"center": v(127.3, 203.2) * mm, "radius": 3.18 * mm});
            skCircle(sketch, "E2.16.4.0", {"center": v(127.41, 177.8) * mm, "radius": 3.18 * mm});
            skCircle(sketch, "E2.16.5.0", {"center": v(127.52, 152.4) * mm, "radius": 3.18 * mm});
            skCircle(sketch, "E2.16.6.0", {"center": v(127.62, 127) * mm, "radius": 3.18 * mm});
            skCircle(sketch, "E2.16.7.0", {"center": v(127.72, 101.6) * mm, "radius": 3.18 * mm});
            skCircle(sketch, "E2.16.8.0", {"center": v(127.83, 76.2) * mm, "radius": 3.18 * mm});
            skCircle(sketch, "E2.16.9.0", {"center": v(127.93, 50.8) * mm, "radius": 3.18 * mm});
            skCircle(sketch, "E2.16.10.0", {"center": v(128.03, 25.4) * mm, "radius": 3.18 * mm});
            skCircle(sketch, "E2.16.11.0", {"center": v(128.14, 0) * mm, "radius": 3.18 * mm});
            skCircle(sketch, "E2.16.12.0", {"center": v(128.24, -25.4) * mm, "radius": 3.18 * mm});
            skCircle(sketch, "E2.16.13.0", {"center": v(128.34, -50.8) * mm, "radius": 3.18 * mm});
            skCircle(sketch, "E2.16.14.0", {"center": v(128.45, -76.2) * mm, "radius": 3.18 * mm});
            skCircle(sketch, "E2.16.15.0", {"center": v(128.55, -101.6) * mm, "radius": 3.18 * mm});
            skCircle(sketch, "E2.16.16.0", {"center": v(128.65, -127) * mm, "radius": 3.18 * mm});
            skCircle(sketch, "E2.16.17.0", {"center": v(128.76, -152.4) * mm, "radius": 3.18 * mm});
            skCircle(sketch, "E2.16.18.0", {"center": v(128.86, -177.8) * mm, "radius": 3.18 * mm});
            skCircle(sketch, "E2.16.19.0", {"center": v(128.96, -203.2) * mm, "radius": 3.18 * mm});
            skCircle(sketch, "E2.16.20.0", {"center": v(129.07, -228.6) * mm, "radius": 3.18 * mm});
            skCircle(sketch, "E2.16.21.0", {"center": v(129.17, -254) * mm, "radius": 3.18 * mm});
            skCircle(sketch, "E2.16.22.0", {"center": v(129.27, -279.4) * mm, "radius": 3.18 * mm});
            skCircle(sketch, "E2.17.0.0", {"center": v(152.4, 279.4) * mm, "radius": 3.18 * mm});
            skCircle(sketch, "E2.17.1.0", {"center": v(152.5, 254) * mm, "radius": 3.18 * mm});
            skCircle(sketch, "E2.17.2.0", {"center": v(152.6, 228.6) * mm, "radius": 3.18 * mm});
            skCircle(sketch, "E2.17.3.0", {"center": v(152.7, 203.2) * mm, "radius": 3.18 * mm});
            skCircle(sketch, "E2.17.4.0", {"center": v(152.81, 177.8) * mm, "radius": 3.18 * mm});
            skCircle(sketch, "E2.17.5.0", {"center": v(152.92, 152.4) * mm, "radius": 3.18 * mm});
            skCircle(sketch, "E2.17.6.0", {"center": v(153.02, 127) * mm, "radius": 3.18 * mm});
            skCircle(sketch, "E2.17.7.0", {"center": v(153.12, 101.6) * mm, "radius": 3.18 * mm});
            skCircle(sketch, "E2.17.8.0", {"center": v(153.23, 76.2) * mm, "radius": 3.18 * mm});
            skCircle(sketch, "E2.17.9.0", {"center": v(153.33, 50.8) * mm, "radius": 3.18 * mm});
            skCircle(sketch, "E2.17.10.0", {"center": v(153.43, 25.4) * mm, "radius": 3.18 * mm});
            skCircle(sketch, "E2.17.11.0", {"center": v(153.54, 0) * mm, "radius": 3.18 * mm});
            skCircle(sketch, "E2.17.12.0", {"center": v(153.64, -25.4) * mm, "radius": 3.18 * mm});
            skCircle(sketch, "E2.17.13.0", {"center": v(153.74, -50.8) * mm, "radius": 3.18 * mm});
            skCircle(sketch, "E2.17.14.0", {"center": v(153.85, -76.2) * mm, "radius": 3.18 * mm});
            skCircle(sketch, "E2.17.15.0", {"center": v(153.95, -101.6) * mm, "radius": 3.18 * mm});
            skCircle(sketch, "E2.17.16.0", {"center": v(154.05, -127) * mm, "radius": 3.18 * mm});
            skCircle(sketch, "E2.17.17.0", {"center": v(154.16, -152.4) * mm, "radius": 3.18 * mm});
            skCircle(sketch, "E2.17.18.0", {"center": v(154.26, -177.8) * mm, "radius": 3.18 * mm});
            skCircle(sketch, "E2.17.19.0", {"center": v(154.36, -203.2) * mm, "radius": 3.18 * mm});
            skCircle(sketch, "E2.17.20.0", {"center": v(154.47, -228.6) * mm, "radius": 3.18 * mm});
            skCircle(sketch, "E2.17.21.0", {"center": v(154.57, -254) * mm, "radius": 3.18 * mm});
            skCircle(sketch, "E2.17.22.0", {"center": v(154.67, -279.4) * mm, "radius": 3.18 * mm});
            skCircle(sketch, "E2.18.0.0", {"center": v(177.8, 279.4) * mm, "radius": 3.18 * mm});
            skCircle(sketch, "E2.18.1.0", {"center": v(177.9, 254) * mm, "radius": 3.18 * mm});
            skCircle(sketch, "E2.18.2.0", {"center": v(178, 228.6) * mm, "radius": 3.18 * mm});
            skCircle(sketch, "E2.18.3.0", {"center": v(178.1, 203.2) * mm, "radius": 3.18 * mm});
            skCircle(sketch, "E2.18.4.0", {"center": v(178.21, 177.8) * mm, "radius": 3.18 * mm});
            skCircle(sketch, "E2.18.5.0", {"center": v(178.32, 152.4) * mm, "radius": 3.18 * mm});
            skCircle(sketch, "E2.18.6.0", {"center": v(178.42, 127) * mm, "radius": 3.18 * mm});
            skCircle(sketch, "E2.18.7.0", {"center": v(178.52, 101.6) * mm, "radius": 3.18 * mm});
            skCircle(sketch, "E2.18.8.0", {"center": v(178.63, 76.2) * mm, "radius": 3.18 * mm});
            skCircle(sketch, "E2.18.9.0", {"center": v(178.73, 50.8) * mm, "radius": 3.18 * mm});
            skCircle(sketch, "E2.18.10.0", {"center": v(178.83, 25.4) * mm, "radius": 3.18 * mm});
            skCircle(sketch, "E2.18.11.0", {"center": v(178.94, 0) * mm, "radius": 3.18 * mm});
            skCircle(sketch, "E2.18.12.0", {"center": v(179.04, -25.4) * mm, "radius": 3.18 * mm});
            skCircle(sketch, "E2.18.13.0", {"center": v(179.14, -50.8) * mm, "radius": 3.18 * mm});
            skCircle(sketch, "E2.18.14.0", {"center": v(179.25, -76.2) * mm, "radius": 3.18 * mm});
            skCircle(sketch, "E2.18.15.0", {"center": v(179.35, -101.6) * mm, "radius": 3.18 * mm});
            skCircle(sketch, "E2.18.16.0", {"center": v(179.45, -127) * mm, "radius": 3.18 * mm});
            skCircle(sketch, "E2.18.17.0", {"center": v(179.56, -152.4) * mm, "radius": 3.18 * mm});
            skCircle(sketch, "E2.18.18.0", {"center": v(179.66, -177.8) * mm, "radius": 3.18 * mm});
            skCircle(sketch, "E2.18.19.0", {"center": v(179.76, -203.2) * mm, "radius": 3.18 * mm});
            skCircle(sketch, "E2.18.20.0", {"center": v(179.87, -228.6) * mm, "radius": 3.18 * mm});
            skCircle(sketch, "E2.18.21.0", {"center": v(179.97, -254) * mm, "radius": 3.18 * mm});
            skCircle(sketch, "E2.18.22.0", {"center": v(180.07, -279.4) * mm, "radius": 3.18 * mm});
            skCircle(sketch, "E2.19.0.0", {"center": v(203.2, 279.4) * mm, "radius": 3.18 * mm});
            skCircle(sketch, "E2.19.1.0", {"center": v(203.3, 254) * mm, "radius": 3.18 * mm});
            skCircle(sketch, "E2.19.2.0", {"center": v(203.4, 228.6) * mm, "radius": 3.18 * mm});
            skCircle(sketch, "E2.19.3.0", {"center": v(203.5, 203.2) * mm, "radius": 3.18 * mm});
            skCircle(sketch, "E2.19.4.0", {"center": v(203.61, 177.8) * mm, "radius": 3.18 * mm});
            skCircle(sketch, "E2.19.5.0", {"center": v(203.72, 152.4) * mm, "radius": 3.18 * mm});
            skCircle(sketch, "E2.19.6.0", {"center": v(203.82, 127) * mm, "radius": 3.18 * mm});
            skCircle(sketch, "E2.19.7.0", {"center": v(203.92, 101.6) * mm, "radius": 3.18 * mm});
            skCircle(sketch, "E2.19.8.0", {"center": v(204.03, 76.2) * mm, "radius": 3.18 * mm});
            skCircle(sketch, "E2.19.9.0", {"center": v(204.13, 50.8) * mm, "radius": 3.18 * mm});
            skCircle(sketch, "E2.19.10.0", {"center": v(204.23, 25.4) * mm, "radius": 3.18 * mm});
            skCircle(sketch, "E2.19.11.0", {"center": v(204.34, 0) * mm, "radius": 3.18 * mm});
            skCircle(sketch, "E2.19.12.0", {"center": v(204.44, -25.4) * mm, "radius": 3.18 * mm});
            skCircle(sketch, "E2.19.13.0", {"center": v(204.54, -50.8) * mm, "radius": 3.18 * mm});
            skCircle(sketch, "E2.19.14.0", {"center": v(204.65, -76.2) * mm, "radius": 3.18 * mm});
            skCircle(sketch, "E2.19.15.0", {"center": v(204.75, -101.6) * mm, "radius": 3.18 * mm});
            skCircle(sketch, "E2.19.16.0", {"center": v(204.85, -127) * mm, "radius": 3.18 * mm});
            skCircle(sketch, "E2.19.17.0", {"center": v(204.96, -152.4) * mm, "radius": 3.18 * mm});
            skCircle(sketch, "E2.19.18.0", {"center": v(205.06, -177.8) * mm, "radius": 3.18 * mm});
            skCircle(sketch, "E2.19.19.0", {"center": v(205.16, -203.2) * mm, "radius": 3.18 * mm});
            skCircle(sketch, "E2.19.20.0", {"center": v(205.27, -228.6) * mm, "radius": 3.18 * mm});
            skCircle(sketch, "E2.19.21.0", {"center": v(205.37, -254) * mm, "radius": 3.18 * mm});
            skCircle(sketch, "E2.19.22.0", {"center": v(205.47, -279.4) * mm, "radius": 3.18 * mm});
            skCircle(sketch, "E2.20.0.0", {"center": v(228.6, 279.4) * mm, "radius": 3.18 * mm});
            skCircle(sketch, "E2.20.1.0", {"center": v(228.7, 254) * mm, "radius": 3.18 * mm});
            skCircle(sketch, "E2.20.2.0", {"center": v(228.8, 228.6) * mm, "radius": 3.18 * mm});
            skCircle(sketch, "E2.20.3.0", {"center": v(228.9, 203.2) * mm, "radius": 3.18 * mm});
            skCircle(sketch, "E2.20.4.0", {"center": v(229.01, 177.8) * mm, "radius": 3.18 * mm});
            skCircle(sketch, "E2.20.5.0", {"center": v(229.12, 152.4) * mm, "radius": 3.18 * mm});
            skCircle(sketch, "E2.20.6.0", {"center": v(229.22, 127) * mm, "radius": 3.18 * mm});
            skCircle(sketch, "E2.20.7.0", {"center": v(229.32, 101.6) * mm, "radius": 3.18 * mm});
            skCircle(sketch, "E2.20.8.0", {"center": v(229.43, 76.2) * mm, "radius": 3.18 * mm});
            skCircle(sketch, "E2.20.9.0", {"center": v(229.53, 50.8) * mm, "radius": 3.18 * mm});
            skCircle(sketch, "E2.20.10.0", {"center": v(229.63, 25.4) * mm, "radius": 3.18 * mm});
            skCircle(sketch, "E2.20.11.0", {"center": v(229.74, 0) * mm, "radius": 3.18 * mm});
            skCircle(sketch, "E2.20.12.0", {"center": v(229.84, -25.4) * mm, "radius": 3.18 * mm});
            skCircle(sketch, "E2.20.13.0", {"center": v(229.94, -50.8) * mm, "radius": 3.18 * mm});
            skCircle(sketch, "E2.20.14.0", {"center": v(230.05, -76.2) * mm, "radius": 3.18 * mm});
            skCircle(sketch, "E2.20.15.0", {"center": v(230.15, -101.6) * mm, "radius": 3.18 * mm});
            skCircle(sketch, "E2.20.16.0", {"center": v(230.25, -127) * mm, "radius": 3.18 * mm});
            skCircle(sketch, "E2.20.17.0", {"center": v(230.36, -152.4) * mm, "radius": 3.18 * mm});
            skCircle(sketch, "E2.20.18.0", {"center": v(230.46, -177.8) * mm, "radius": 3.18 * mm});
            skCircle(sketch, "E2.20.19.0", {"center": v(230.56, -203.2) * mm, "radius": 3.18 * mm});
            skCircle(sketch, "E2.20.20.0", {"center": v(230.67, -228.6) * mm, "radius": 3.18 * mm});
            skCircle(sketch, "E2.20.21.0", {"center": v(230.77, -254) * mm, "radius": 3.18 * mm});
            skCircle(sketch, "E2.20.22.0", {"center": v(230.87, -279.4) * mm, "radius": 3.18 * mm});
            skCircle(sketch, "E2.21.0.0", {"center": v(254, 279.4) * mm, "radius": 3.18 * mm});
            skCircle(sketch, "E2.21.1.0", {"center": v(254.1, 254) * mm, "radius": 3.18 * mm});
            skCircle(sketch, "E2.21.2.0", {"center": v(254.2, 228.6) * mm, "radius": 3.18 * mm});
            skCircle(sketch, "E2.21.3.0", {"center": v(254.3, 203.2) * mm, "radius": 3.18 * mm});
            skCircle(sketch, "E2.21.4.0", {"center": v(254.41, 177.8) * mm, "radius": 3.18 * mm});
            skCircle(sketch, "E2.21.5.0", {"center": v(254.52, 152.4) * mm, "radius": 3.18 * mm});
            skCircle(sketch, "E2.21.6.0", {"center": v(254.62, 127) * mm, "radius": 3.18 * mm});
            skCircle(sketch, "E2.21.7.0", {"center": v(254.72, 101.6) * mm, "radius": 3.18 * mm});
            skCircle(sketch, "E2.21.8.0", {"center": v(254.83, 76.2) * mm, "radius": 3.18 * mm});
            skCircle(sketch, "E2.21.9.0", {"center": v(254.93, 50.8) * mm, "radius": 3.18 * mm});
            skCircle(sketch, "E2.21.10.0", {"center": v(255.03, 25.4) * mm, "radius": 3.18 * mm});
            skCircle(sketch, "E2.21.11.0", {"center": v(255.14, 0) * mm, "radius": 3.18 * mm});
            skCircle(sketch, "E2.21.12.0", {"center": v(255.24, -25.4) * mm, "radius": 3.18 * mm});
            skCircle(sketch, "E2.21.13.0", {"center": v(255.34, -50.8) * mm, "radius": 3.18 * mm});
            skCircle(sketch, "E2.21.14.0", {"center": v(255.45, -76.2) * mm, "radius": 3.18 * mm});
            skCircle(sketch, "E2.21.15.0", {"center": v(255.55, -101.6) * mm, "radius": 3.18 * mm});
            skCircle(sketch, "E2.21.16.0", {"center": v(255.65, -127) * mm, "radius": 3.18 * mm});
            skCircle(sketch, "E2.21.17.0", {"center": v(255.76, -152.4) * mm, "radius": 3.18 * mm});
            skCircle(sketch, "E2.21.18.0", {"center": v(255.86, -177.8) * mm, "radius": 3.18 * mm});
            skCircle(sketch, "E2.21.19.0", {"center": v(255.96, -203.2) * mm, "radius": 3.18 * mm});
            skCircle(sketch, "E2.21.20.0", {"center": v(256.07, -228.6) * mm, "radius": 3.18 * mm});
            skCircle(sketch, "E2.21.21.0", {"center": v(256.17, -254) * mm, "radius": 3.18 * mm});
            skCircle(sketch, "E2.21.22.0", {"center": v(256.27, -279.4) * mm, "radius": 3.18 * mm});
            skCircle(sketch, "E2.22.0.0", {"center": v(279.4, 279.4) * mm, "radius": 3.18 * mm});
            skCircle(sketch, "E2.22.1.0", {"center": v(279.5, 254) * mm, "radius": 3.18 * mm});
            skCircle(sketch, "E2.22.2.0", {"center": v(279.6, 228.6) * mm, "radius": 3.18 * mm});
            skCircle(sketch, "E2.22.3.0", {"center": v(279.7, 203.2) * mm, "radius": 3.18 * mm});
            skCircle(sketch, "E2.22.4.0", {"center": v(279.81, 177.8) * mm, "radius": 3.18 * mm});
            skCircle(sketch, "E2.22.5.0", {"center": v(279.92, 152.4) * mm, "radius": 3.18 * mm});
            skCircle(sketch, "E2.22.6.0", {"center": v(280.02, 127) * mm, "radius": 3.18 * mm});
            skCircle(sketch, "E2.22.7.0", {"center": v(280.12, 101.6) * mm, "radius": 3.18 * mm});
            skCircle(sketch, "E2.22.8.0", {"center": v(280.23, 76.2) * mm, "radius": 3.18 * mm});
            skCircle(sketch, "E2.22.9.0", {"center": v(280.33, 50.8) * mm, "radius": 3.18 * mm});
            skCircle(sketch, "E2.22.10.0", {"center": v(280.43, 25.4) * mm, "radius": 3.18 * mm});
            skCircle(sketch, "E2.22.11.0", {"center": v(280.54, 0) * mm, "radius": 3.18 * mm});
            skCircle(sketch, "E2.22.12.0", {"center": v(280.64, -25.4) * mm, "radius": 3.18 * mm});
            skCircle(sketch, "E2.22.13.0", {"center": v(280.74, -50.8) * mm, "radius": 3.18 * mm});
            skCircle(sketch, "E2.22.14.0", {"center": v(280.85, -76.2) * mm, "radius": 3.18 * mm});
            skCircle(sketch, "E2.22.15.0", {"center": v(280.95, -101.6) * mm, "radius": 3.18 * mm});
            skCircle(sketch, "E2.22.16.0", {"center": v(281.05, -127) * mm, "radius": 3.18 * mm});
            skCircle(sketch, "E2.22.17.0", {"center": v(281.16, -152.4) * mm, "radius": 3.18 * mm});
            skCircle(sketch, "E2.22.18.0", {"center": v(281.26, -177.8) * mm, "radius": 3.18 * mm});
            skCircle(sketch, "E2.22.19.0", {"center": v(281.36, -203.2) * mm, "radius": 3.18 * mm});
            skCircle(sketch, "E2.22.20.0", {"center": v(281.47, -228.6) * mm, "radius": 3.18 * mm});
            skCircle(sketch, "E2.22.21.0", {"center": v(281.57, -254) * mm, "radius": 3.18 * mm});
            skCircle(sketch, "E2.22.22.0", {"center": v(281.67, -279.4) * mm, "radius": 3.18 * mm});
            skLineSegment(sketch, "E2.direction1", {"start": v(-279.4, 279.4) * mm, "end": v(-254, 279.4) * mm, "construction": true});
            skLineSegment(sketch, "E2.direction2", {"start": v(-279.4, 279.4) * mm, "end": v(-279.3, 254) * mm, "construction": true});
            skSolve(sketch);
        }
        {
            var Q0;
            Q0=makeQuery(id+"F0.imprint","IMPRINT",FACE,{"disambiguationData":[TD([[makeQuery(id+"F0.imprint","IMPRINT",EDGE,{"derivedFrom":sQuery(id+"F0.wireOp",EDGE,"E0.rect.bottom")}),1.0]])]});
            extrude(context, id + "F1", {"entities" : qUnion([Q0]), "depth" : 3.17 * mm});
        }
    });
